# Revit family: Shelf_Wall_Mount-Bradley_Corp-Elvari-7B2_Series_5Dx12L
name_source: partatom
category: Specialty Equipment
units: mm (PartAtom-declared; Revit-internal decimal feet)

## family parameters
Always vertical = No
Cut with Voids When Loaded = No
Enable Cutting in Views = No
Maintain Annotation Orientation = No
Part Type = Normal
Room Calculation Point = No
Round Connector Dimension = Use Diameter
Shared = No
Work Plane-Based = No

## types (2) — shared parameters
Default Elevation = 0' - 0"
Design Status = 1
Manufacturer = Bradley Corporation
Product Page URL = https://www.bradleycorp.com
Product Tech Data URL - English = https://www.bradleycorp.com
Specifications URL = https://www.bradleycorp.com

## per-type parameters (varying)
| type | Description | Hooks | Model |
| 7B2-0051296-Hooks | 5"D x 12"L SHELF WITH HOOKS | Yes | 7B2-0051296 |
| 7B2-0051200-No Hooks | 5"D x 12"L SHELF NO HOOKS | No | 7B2-0051200 |

## geometry (parser evidence)
native form markers: Blend x4, Sweep x8
no freeform markers — native parametric forms only
